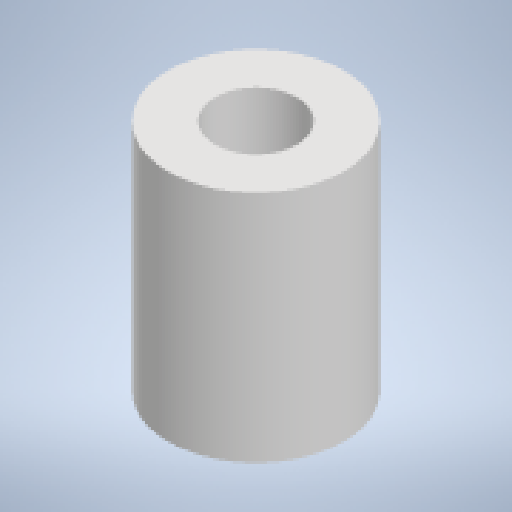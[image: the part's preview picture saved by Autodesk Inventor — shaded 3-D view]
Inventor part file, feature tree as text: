
AUTODESK INVENTOR PART (.ipt)
format: ipt  version: 2024.2 (Build 282272000, 272)  size: 139,264 bytes
history: native  units: mm
features: revolve x1
ambient origin geometry x8: Origin, YZ Plane, XZ Plane, XY Plane, X Axis, Y Axis, Z Axis, Center Point
bodies: Solid1 (feature_tree)
feature tree (1):
  revolve  "Revolution1"  Angle=90.0deg
